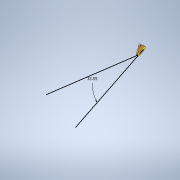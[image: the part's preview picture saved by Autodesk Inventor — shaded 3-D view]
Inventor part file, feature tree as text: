
AUTODESK INVENTOR PART (.ipt)
format: ipt  version: 2020 (Build 240168000, 168)  size: 126,464 bytes
history: native  units: mm
features: other x3, sketch x1
ambient origin geometry x8: Origin, YZ Plane, XZ Plane, XY Plane, X Axis, Y Axis, Z Axis, Center Point
bodies: Solid1 (feature_tree)
feature tree (4):
  other  "Kauri modular camera mount HDzero micro v1.ipt"
  sketch  "Sketch1"  dims[d0=10.0mm d1=5.85558mm]
  other  "Solid1::Kauri modular camera mount HDzero micro v1.ipt"
  other  "TaggingFeature1"
